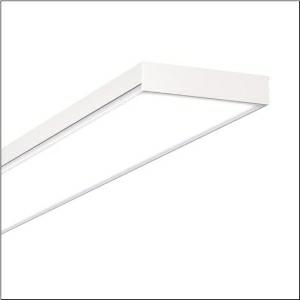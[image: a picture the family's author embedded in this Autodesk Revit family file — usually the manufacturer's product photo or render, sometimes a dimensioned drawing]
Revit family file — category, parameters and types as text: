
# Revit family: apollon_r__31_51mp26wd2441w_9318
name_source: partatom
category: Lighting Fixtures
units: mm (PartAtom-declared; Revit-internal decimal feet)

## family parameters
Cut with Voids When Loaded = No
Host = Face
Light Source = No
Part Type = Normal
Room Calculation Point = No
Round Connector Dimension = Use Diameter
Shared = No

## types (1)
- Apollon® 31 (1 x LED, 4600 lm, 33 W, 4000K)
    Apparent Load = 33 VA
    CIE Flux Codes = 61 87 97 97 100
    Color Rendering = 80
    Color Temperature = 4000K
    Default Elevation = 1800 mm
    Description = Apollon® 31, office luminaire, primary optical cover: micro prismatic cover, of PMMA, light emission: direct distribution, primary light characteristic: symmetric, installation type: surface-mounted, LED, rated luminous flux: 4.600lm, luminous efficacy: 139lm/W, light colour: 840, colour temperature: 4000K, control gear: ECG DALI, with terminal, 5-pole, mains connection: 220..240V, AC, 50/60Hz, rated input power: 33W, housing, of sheet steel, coil coated, traffic white (RAL 9016), length: 1.545mm, width: 200mm, height: 44mm, protection rating (complete): IP20, insulation class (complete): insulation class II (safety insulation), certification: CE, impact resistance: IK02, permissible operating ambient temperature: -20..+40°C, standard: EN 60598-2-22, packaging unit: 1 piece
    Height = 44 mm
    Lamp = 1 x LED
    Lamp Light Flux = 4600 lm
    Lamp Power = 33 W
    Lamp count = 1
    Length = 1545 mm
    Luminous efficacy = 139 lm/W
    Manufacturer = Siteco
    ModVariant = No
    Model = 51MP26WD2441W
    Mounting Place = Ceiling
    Mounting Type = Surface mounted
    Number of Poles = 1
    OnlyDefault = Yes
    Power Factor = 1
    Product Name = Apollon® 31
    Product group = office luminaire | ceiling mounted
    ProductGroupID = 302
    Protection Class = Protection class II
    Protection Degree = IP 20
    RLX_Detail_Level = 1
    RlxData = <blob elided: 20741 chars, md5=c51f515d>
    Socket = socket
    Standby Power = 0 W
    System Light Flux = 4600 lm
    System Power = 33 W
    Type Comments = Product without accessories
    Type Image = l_1007095.jpg
    URL = http://relux.com
    VarID = ---
    Voltage = 0 V
    Weight = 0.00 kg
    Width = 200 mm  [stored 0.656168 ft]

note: [stored X ft] marks values corroborated as IEEE doubles in the binary element streams (Revit-internal decimal feet)

## geometry (parser evidence)
native form markers: Blend x4, Sweep x12
no freeform markers — native parametric forms only
